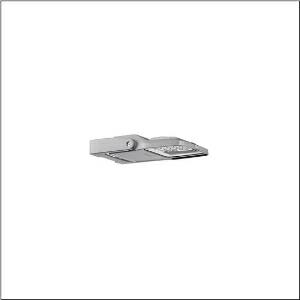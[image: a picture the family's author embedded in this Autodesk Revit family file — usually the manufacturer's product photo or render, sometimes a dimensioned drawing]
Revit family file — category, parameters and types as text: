
# Revit family: floodlight_fl_21_iq_micro___pl33t_5xa7761a2f2a_98c0
name_source: partatom
category: Lighting Fixtures
units: mm (PartAtom-declared; Revit-internal decimal feet)

## family parameters
Cut with Voids When Loaded = No
Host = Face
Light Source = No
Part Type = Normal
Room Calculation Point = No
Round Connector Dimension = Use Diameter
Shared = No

## types (1)
- --- (1 x LED, 2930 lm, 23.1 W, 3000K)
    Apparent Load = 23 VA
    CIE Flux Codes = 26 75 99 100 100
    Color Rendering = 70
    Color Temperature = 3000K
    Default Elevation = 1800 mm
    Description = Floodlight FL 21 iQ micro, floodlight, primary light control with lens, of PMMA, primary optical cover: protective disc, of toughened safety glass, transparent, light distribution: PL33T, light emission: direct distribution, installation type: surface-mounted, LED, High Power LED, rated luminous flux: 2.930lm, luminous efficacy: 127lm/W, light colour: 730, colour temperature: 3000K, control gear: iQ Comfort/DALI, control: optimised constant luminous flux control (CLO 2.0), Desk-Remote (wireless, voltage-free reading and setting of iQ features in the workshop via application-optimized NFC function/RFID function), Light-Fading, Smart-Wire, Night-Set, Lumen-Switch, Temp-Guard, Auto-Match, with terminal, 6-pole, mains connection: 220..240V, AC, 50/60Hz, start of lifetime: 23W, end of service life: 24W, reduction: 11W, luminaire housing, of diecast aluminium, powder-coated, Siteco® metallic grey (DB 702S), corrosivity category C5 mid according to DIN EN ISO 12944, suitable for swimming pools, chlorine-resistant, sealing non-destructively replaceable, design bracket, of diecast aluminium, powder-coated, Siteco® metallic grey (DB 702S), protection rating (complete): IP66, insulation class (complete): insulation class II (safety insulation), certification: CE, ENEC, VDE, protection symbol: D, impact resistance: IK07, permissible operating ambient temperature: -40..+40°C, permissible operating ambient temperature for outdoor applications: -40..+50°C, standard: DIN EN 12944, LABS conformity tested according to VDMA 24364:2018-05, packaging unit: 1 piece

Light Distribution: PL33T
    Height = 65 mm
    Lamp = 1 x LED
    Lamp Light Flux = 2930 lm
    Lamp Power = 23.1 W
    Lamp count = 1
    Length = 312 mm
    Luminous efficacy = 127 lm/W
    Manufacturer = Siteco
    ModVariant = No
    Model = 5XA7761A2F2A
    Mounting Place = Wall
    Mounting Type = Surface mounted
    Number of Poles = 1
    OnlyDefault = Yes
    Power Factor = 1
    Product Name = Floodlight FL 21 iQ micro | PL33T
    Product group = floodlight | wall mounted
    ProductGroupID = 2001
    Protection Class = Protection class II
    Protection Degree = IP 66
    RLX_Detail_Level = 1
    RLX_Emergency_Light_Flux = 0 lm
    RLX_Emergency_Type = 0
    RLX_Emergency_Type_DB = No
    RlxData = <blob elided: 97361 chars, md5=f88022de>
    Socket = socket
    Standby Power = 0 W
    System Light Flux = 2930 lm
    System Power = 23 W
    Type Comments = factory setting: luminous flux: 100 % | dim-lin: 254 | 455 mA
    Type Image = l_1006878.jpg
    URL = http://relux.com
    VarID = @adj_169695
    Voltage = 0 V
    Weight = 0.00 kg
    Width = 230 mm

## geometry (parser evidence)
native form markers: Blend x4, Sweep x10
no freeform markers — native parametric forms only
